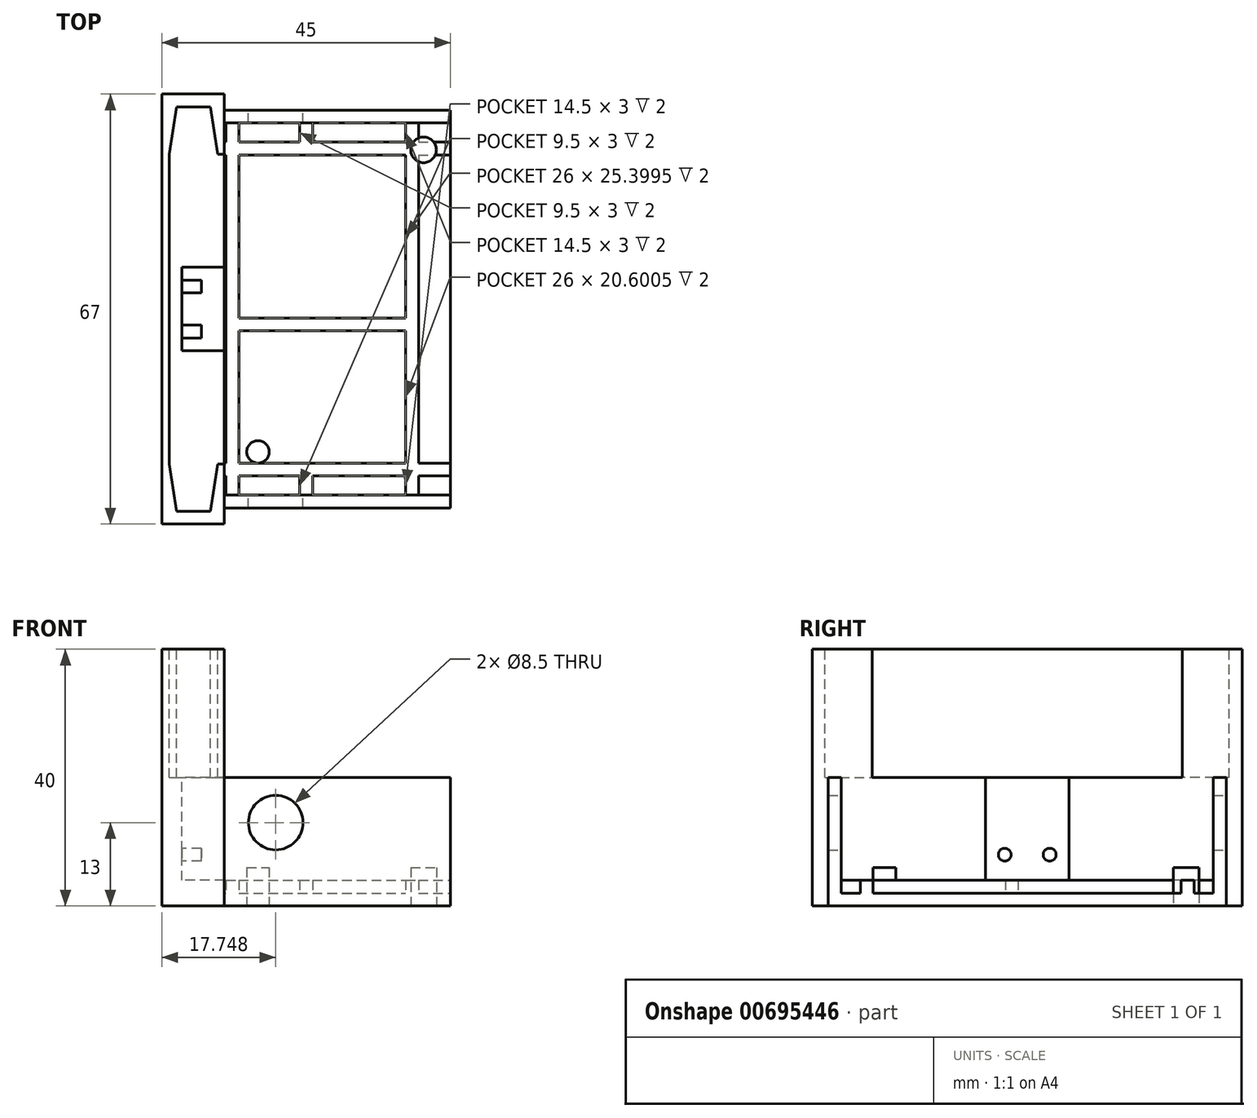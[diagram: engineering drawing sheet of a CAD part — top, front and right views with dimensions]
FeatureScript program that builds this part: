
annotation { "Feature Type Name" : "Feature", "Feature Type Description" : "" }
export const myFeature = defineFeature(function(context is Context, id is Id, definition is map)
    precondition{}
    {
        {
            var Q0;
            Q0=qCreatedBy(makeId("Top.planeOp"),FACE);
            var sketch = newSketch(context, id + "F0", { "sketchPlane" : qUnion([Q0])});
            skLineSegment(sketch, "E0.bottom", {"start": v(-32.76, -1.06) * mm, "end": v(12.24, -1.06) * mm});
            skLineSegment(sketch, "E0.top", {"start": v(-32.76, -63.06) * mm, "end": v(12.24, -63.06) * mm});
            skLineSegment(sketch, "E0.left", {"start": v(-32.76, -1.06) * mm, "end": v(-32.76, -63.06) * mm});
            skLineSegment(sketch, "E0.right", {"start": v(12.24, -1.06) * mm, "end": v(12.24, -63.06) * mm});
            skSolve(sketch);
        }
        {
            var Q0;
            Q0 = qSketchRegion(id + "F0", true);
            extrude(context, id + "F1", {"entities" : qUnion([Q0]), "depth" : 2 * mm, "offsetDistance" : 25 * mm});
        }
        {
            var Q0;
            Q0=makeQuery(id+"F1.opExtrude","CAP_FACE",FACE,{"disambiguationData":[OSD([sQuery(id+"F0.wireOp",EDGE,"E0.bottom"),sQuery(id+"F0.wireOp",EDGE,"E0.top"),sQuery(id+"F0.wireOp",EDGE,"E0.left"),sQuery(id+"F0.wireOp",EDGE,"E0.right")])],"isStart":false});
            var sketch = newSketch(context, id + "F2", { "sketchPlane" : qUnion([Q0])});
            skLineSegment(sketch, "E1.bottom", {"start": v(-32.76, -58.06) * mm, "end": v(12.24, -58.06) * mm});
            skLineSegment(sketch, "E1.top", {"start": v(-32.76, -56.06) * mm, "end": v(12.24, -56.06) * mm});
            skLineSegment(sketch, "E1.left", {"start": v(-32.76, -58.06) * mm, "end": v(-32.76, -56.06) * mm});
            skLineSegment(sketch, "E1.right", {"start": v(12.24, -58.06) * mm, "end": v(12.24, -56.06) * mm});
            skLineSegment(sketch, "E2.bottom", {"start": v(-22.76, -1.06) * mm, "end": v(-20.76, -1.06) * mm});
            skLineSegment(sketch, "E2.top", {"start": v(-22.76, -63.06) * mm, "end": v(-20.76, -63.06) * mm});
            skLineSegment(sketch, "E2.left", {"start": v(-22.76, -1.06) * mm, "end": v(-22.76, -63.06) * mm});
            skLineSegment(sketch, "E2.right", {"start": v(-20.76, -1.06) * mm, "end": v(-20.76, -63.06) * mm});
            skLineSegment(sketch, "E3.bottom", {"start": v(-11.26, -1.06) * mm, "end": v(-9.26, -1.06) * mm});
            skLineSegment(sketch, "E3.top", {"start": v(-11.26, -63.06) * mm, "end": v(-9.26, -63.06) * mm});
            skLineSegment(sketch, "E3.left", {"start": v(-11.26, -1.06) * mm, "end": v(-11.26, -63.06) * mm});
            skLineSegment(sketch, "E3.right", {"start": v(-9.26, -1.06) * mm, "end": v(-9.26, -63.06) * mm});
            skLineSegment(sketch, "E4.bottom", {"start": v(5.24, -1.06) * mm, "end": v(7.24, -1.06) * mm});
            skLineSegment(sketch, "E4.top", {"start": v(5.24, -63.06) * mm, "end": v(7.24, -63.06) * mm});
            skLineSegment(sketch, "E4.left", {"start": v(5.24, -1.06) * mm, "end": v(5.24, -63.06) * mm});
            skLineSegment(sketch, "E4.right", {"start": v(7.24, -1.06) * mm, "end": v(7.24, -63.06) * mm});
            skLineSegment(sketch, "E5.bottom", {"start": v(-32.76, -8.06) * mm, "end": v(12.24, -8.06) * mm});
            skLineSegment(sketch, "E5.top", {"start": v(-32.76, -6.06) * mm, "end": v(12.24, -6.06) * mm});
            skLineSegment(sketch, "E5.left", {"start": v(-32.76, -8.06) * mm, "end": v(-32.76, -6.06) * mm});
            skLineSegment(sketch, "E5.right", {"start": v(12.24, -8.06) * mm, "end": v(12.24, -6.06) * mm});
            skSolve(sketch);
        }
        {
            var Q0;
            Q0 = qSketchRegion(id + "F2", true);
            extrude(context, id + "F3", {"entities" : qUnion([Q0]), "operationType" : NewBodyOperationType.ADD, "depth" : 2 * mm, "offsetDistance" : 25 * mm});
        }
        {
            var Q0;
            Q0=makeQuery(id+"F1.opExtrude","CAP_FACE",FACE,{"disambiguationData":[OSD([sQuery(id+"F0.wireOp",EDGE,"E0.bottom"),sQuery(id+"F0.wireOp",EDGE,"E0.top"),sQuery(id+"F0.wireOp",EDGE,"E0.left"),sQuery(id+"F0.wireOp",EDGE,"E0.right")])],"isStart":true});
            var sketch = newSketch(context, id + "F4", { "sketchPlane" : qUnion([Q0])});
            skCircle(sketch, "E6", {"center": v(-17.76, 54.3) * mm, "radius": 1.75 * mm});
            skCircle(sketch, "E7", {"center": v(8.04, 7.26) * mm, "radius": 2 * mm});
            skSolve(sketch);
        }
        {
            var Q0;
            Q0 = qSketchRegion(id + "F4", true);
            extrude(context, id + "F5", {"entities" : qUnion([Q0]), "oppositeDirection" : true, "depth" : 6 * mm, "offsetDistance" : 25 * mm});
        }
        {
            var Q0;
            {var subQ1=sQuery(id+"F2.wireOp",EDGE,"E1.top");var subQ7=sQuery(id+"F2.wireOp",EDGE,"E2.right");var subQ8=makeQuery(id+"F2.imprint","INTERSECT",VERTEX,{"derivedFrom":[subQ1,subQ7]});Q0=makeQuery(id+"F3.boolean.opBoolean","SPLIT",FACE,{"disambiguationData":[TD([makeQuery(id+"F3.opExtrude","SWEPT_FACE",FACE,{"disambiguationData":[OSD([subQ7]),TDD([makeQuery(id+"F2.imprint","IMPRINT",EDGE,{"disambiguationData":[TD([[subQ8,1.0]])],"derivedFrom":subQ7})])]})])],"derivedFrom":makeQuery(id+"F1.opExtrude","CAP_FACE",FACE,{"disambiguationData":[OSD([sQuery(id+"F0.wireOp",EDGE,"E0.bottom"),sQuery(id+"F0.wireOp",EDGE,"E0.top"),sQuery(id+"F0.wireOp",EDGE,"E0.left"),sQuery(id+"F0.wireOp",EDGE,"E0.right")])],"isStart":false})});}
            var sketch = newSketch(context, id + "F6", { "sketchPlane" : qUnion([Q0])});
            skLineSegment(sketch, "E8.bottom", {"start": v(-20.76, -35.46) * mm, "end": v(5.24, -35.46) * mm});
            skLineSegment(sketch, "E8.top", {"start": v(-20.76, -33.46) * mm, "end": v(5.24, -33.46) * mm});
            skLineSegment(sketch, "E8.left", {"start": v(-20.76, -35.46) * mm, "end": v(-20.76, -33.46) * mm});
            skLineSegment(sketch, "E8.right", {"start": v(5.24, -35.46) * mm, "end": v(5.24, -33.46) * mm});
            skSolve(sketch);
        }
        {
            var Q0;
            Q0 = qSketchRegion(id + "F6", true);
            extrude(context, id + "F7", {"entities" : qUnion([Q0]), "operationType" : NewBodyOperationType.ADD, "depth" : 2 * mm, "offsetDistance" : 25 * mm});
        }
        {
            var Q0;
            Q0=makeQuery(id+"F1.opExtrude","CAP_FACE",FACE,{"disambiguationData":[OSD([sQuery(id+"F0.wireOp",EDGE,"E0.bottom"),sQuery(id+"F0.wireOp",EDGE,"E0.top"),sQuery(id+"F0.wireOp",EDGE,"E0.left"),sQuery(id+"F0.wireOp",EDGE,"E0.right")])],"isStart":true});
            var sketch = newSketch(context, id + "F8", { "sketchPlane" : qUnion([Q0])});
            skLineSegment(sketch, "E9.bottom", {"start": v(12.24, 63.06) * mm, "end": v(-32.76, 63.06) * mm});
            skLineSegment(sketch, "E9.top", {"start": v(12.24, 61.06) * mm, "end": v(-32.76, 61.06) * mm});
            skLineSegment(sketch, "E9.left", {"start": v(12.24, 63.06) * mm, "end": v(12.24, 61.06) * mm});
            skLineSegment(sketch, "E9.right", {"start": v(-32.76, 63.06) * mm, "end": v(-32.76, 61.06) * mm});
            skLineSegment(sketch, "E10.bottom", {"start": v(12.24, 1.06) * mm, "end": v(-32.76, 1.06) * mm});
            skLineSegment(sketch, "E10.top", {"start": v(12.24, 3.06) * mm, "end": v(-32.76, 3.06) * mm});
            skLineSegment(sketch, "E10.left", {"start": v(12.24, 1.06) * mm, "end": v(12.24, 3.06) * mm});
            skLineSegment(sketch, "E10.right", {"start": v(-32.76, 1.06) * mm, "end": v(-32.76, 3.06) * mm});
            skSolve(sketch);
        }
        {
            var Q0;
            Q0 = qSketchRegion(id + "F8", true);
            extrude(context, id + "F9", {"entities" : qUnion([Q0]), "operationType" : NewBodyOperationType.ADD, "oppositeDirection" : true, "depth" : 20 * mm, "offsetDistance" : 25 * mm});
        }
        {
            var Q0;
            Q0=makeQuery(id+"F1.opExtrude","CAP_FACE",FACE,{"disambiguationData":[OSD([sQuery(id+"F0.wireOp",EDGE,"E0.bottom"),sQuery(id+"F0.wireOp",EDGE,"E0.top"),sQuery(id+"F0.wireOp",EDGE,"E0.left"),sQuery(id+"F0.wireOp",EDGE,"E0.right")])],"isStart":true});
            var sketch = newSketch(context, id + "F10", { "sketchPlane" : qUnion([Q0])});
            skLineSegment(sketch, "E11.bottom", {"start": v(-32.76, -1.44) * mm, "end": v(-23.01, -1.44) * mm});
            skLineSegment(sketch, "E11.top", {"start": v(-23.01, 65.56) * mm, "end": v(-32.76, 65.56) * mm});
            skLineSegment(sketch, "E11.left", {"start": v(-32.76, -1.44) * mm, "end": v(-32.76, 65.56) * mm});
            skLineSegment(sketch, "E11.right", {"start": v(-23.01, -1.44) * mm, "end": v(-23.01, 65.56) * mm});
            skSolve(sketch);
        }
        {
            var Q0;
            Q0 = qSketchRegion(id + "F10", true);
            extrude(context, id + "F11", {"entities" : qUnion([Q0]), "operationType" : NewBodyOperationType.ADD, "oppositeDirection" : true, "depth" : 40 * mm, "offsetDistance" : 25 * mm});
        }
        {
            var Q0;
            Q0=makeQuery(id+"F11.opExtrude","CAP_FACE",FACE,{"disambiguationData":[OSD([sQuery(id+"F10.wireOp",EDGE,"E11.bottom"),sQuery(id+"F10.wireOp",EDGE,"E11.top"),sQuery(id+"F10.wireOp",EDGE,"E11.left"),sQuery(id+"F10.wireOp",EDGE,"E11.right")])],"isStart":false});
            var sketch = newSketch(context, id + "F12", { "sketchPlane" : qUnion([Q0])});
            skLineSegment(sketch, "E12", {"start": v(-31.6, -56.2) * mm, "end": v(-31.6, -7.92) * mm});
            skLineSegment(sketch, "E13", {"start": v(-31.6, -7.92) * mm, "end": v(-30.45, -0.56) * mm});
            skLineSegment(sketch, "E14", {"start": v(-30.45, -0.56) * mm, "end": v(-25.16, -0.56) * mm});
            skLineSegment(sketch, "E15", {"start": v(-25.16, -0.56) * mm, "end": v(-24.01, -7.92) * mm});
            skLineSegment(sketch, "E16", {"start": v(-24.01, -7.92) * mm, "end": v(-24.01, -56.2) * mm});
            skLineSegment(sketch, "E17", {"start": v(-24.01, -56.2) * mm, "end": v(-25.16, -63.56) * mm});
            skLineSegment(sketch, "E18", {"start": v(-25.16, -63.56) * mm, "end": v(-30.45, -63.56) * mm});
            skLineSegment(sketch, "E19", {"start": v(-30.45, -63.56) * mm, "end": v(-31.6, -56.2) * mm});
            skLineSegment(sketch, "E20.bottom", {"start": v(-24.01, -56.2) * mm, "end": v(-23.01, -56.2) * mm});
            skLineSegment(sketch, "E20.top", {"start": v(-24.01, -7.92) * mm, "end": v(-23.01, -7.92) * mm});
            skLineSegment(sketch, "E20.left", {"start": v(-24.01, -56.2) * mm, "end": v(-24.01, -7.92) * mm});
            skLineSegment(sketch, "E20.right", {"start": v(-23.01, -56.2) * mm, "end": v(-23.01, -7.92) * mm});
            skSolve(sketch);
        }
        {
            var Q0;
            Q0 = qSketchRegion(id + "F12", true);
            extrude(context, id + "F13", {"entities" : qUnion([Q0]), "operationType" : NewBodyOperationType.REMOVE, "oppositeDirection" : true, "depth" : 20 * mm, "offsetDistance" : 25 * mm});
        }
        {
            var Q0;
            Q0=makeQuery(id+"F13.boolean.opBoolean","COPY",FACE,{"derivedFrom":makeQuery(id+"F13.opExtrude","CAP_FACE",FACE,{"disambiguationData":[OSD([sQuery(id+"F12.wireOp",EDGE,"E12"),sQuery(id+"F12.wireOp",EDGE,"E13"),sQuery(id+"F12.wireOp",EDGE,"E14"),sQuery(id+"F12.wireOp",EDGE,"E15"),sQuery(id+"F12.wireOp",EDGE,"E17"),sQuery(id+"F12.wireOp",EDGE,"E18"),sQuery(id+"F12.wireOp",EDGE,"E19"),sQuery(id+"F12.wireOp",EDGE,"E20.bottom"),sQuery(id+"F12.wireOp",EDGE,"E20.top"),sQuery(id+"F12.wireOp",EDGE,"E20.right")])],"isStart":false})});
            var sketch = newSketch(context, id + "F14", { "sketchPlane" : qUnion([Q0])});
            skLineSegment(sketch, "E21.bottom", {"start": v(-23.01, -38.56) * mm, "end": v(-29.6, -38.56) * mm});
            skLineSegment(sketch, "E21.top", {"start": v(-23.01, -25.56) * mm, "end": v(-29.6, -25.56) * mm});
            skLineSegment(sketch, "E21.left", {"start": v(-23.01, -38.56) * mm, "end": v(-23.01, -25.56) * mm});
            skLineSegment(sketch, "E21.right", {"start": v(-29.6, -38.56) * mm, "end": v(-29.6, -25.56) * mm});
            skSolve(sketch);
        }
        {
            var Q0;
            Q0 = qSketchRegion(id + "F14", true);
            extrude(context, id + "F15", {"entities" : qUnion([Q0]), "operationType" : NewBodyOperationType.REMOVE, "oppositeDirection" : true, "depth" : 16 * mm, "offsetDistance" : 25 * mm});
        }
        {
            var Q0;
            Q0=makeQuery(id+"F9.boolean.opBoolean","MERGE",FACE,{"derivedFrom":[makeQuery(id+"F3.boolean.opBoolean","MERGE",FACE,{"derivedFrom":[makeQuery(id+"F1.opExtrude","SWEPT_FACE",FACE,{"disambiguationData":[OSD([sQuery(id+"F0.wireOp",EDGE,"E0.bottom")])]}),makeQuery(id+"F3.opExtrude","SWEPT_FACE",FACE,{"disambiguationData":[OSD([sQuery(id+"F2.wireOp",EDGE,"E2.bottom")])]}),makeQuery(id+"F3.opExtrude","SWEPT_FACE",FACE,{"disambiguationData":[OSD([sQuery(id+"F2.wireOp",EDGE,"E3.bottom")])]}),makeQuery(id+"F3.opExtrude","SWEPT_FACE",FACE,{"disambiguationData":[OSD([sQuery(id+"F2.wireOp",EDGE,"E4.bottom")])]})]}),makeQuery(id+"F9.opExtrude","SWEPT_FACE",FACE,{"disambiguationData":[OSD([sQuery(id+"F8.wireOp",EDGE,"E10.bottom")])]})]});
            var sketch = newSketch(context, id + "F16", { "sketchPlane" : qUnion([Q0])});
            skCircle(sketch, "E22", {"center": v(15.01, 13) * mm, "radius": 4.25 * mm});
            skPoint(sketch, "E22.centerSnap0", {"position": v(21.01, 13) * mm});
            skSolve(sketch);
        }
        {
            var Q0;
            Q0 = qSketchRegion(id + "F16", true);
            extrude(context, id + "F17", {"entities" : qUnion([Q0]), "operationType" : NewBodyOperationType.REMOVE, "oppositeDirection" : true, "depth" : 70 * mm, "offsetDistance" : 25 * mm});
        }
        {
            var Q0;
            Q0=makeQuery(id+"F15.boolean.opBoolean","COPY",FACE,{"derivedFrom":makeQuery(id+"F15.opExtrude","SWEPT_FACE",FACE,{"disambiguationData":[OSD([sQuery(id+"F14.wireOp",EDGE,"E21.right")])]})});
            var sketch = newSketch(context, id + "F18", { "sketchPlane" : qUnion([Q0])});
            skCircle(sketch, "E23", {"center": v(-35.56, 8) * mm, "radius": 1 * mm});
            skCircle(sketch, "E24", {"center": v(-28.56, 8) * mm, "radius": 1 * mm});
            skSolve(sketch);
        }
        {
            var Q0;
            Q0 = qSketchRegion(id + "F18", true);
            extrude(context, id + "F19", {"entities" : qUnion([Q0]), "operationType" : NewBodyOperationType.ADD, "depth" : 3 * mm, "offsetDistance" : 25 * mm});
        }
    });
